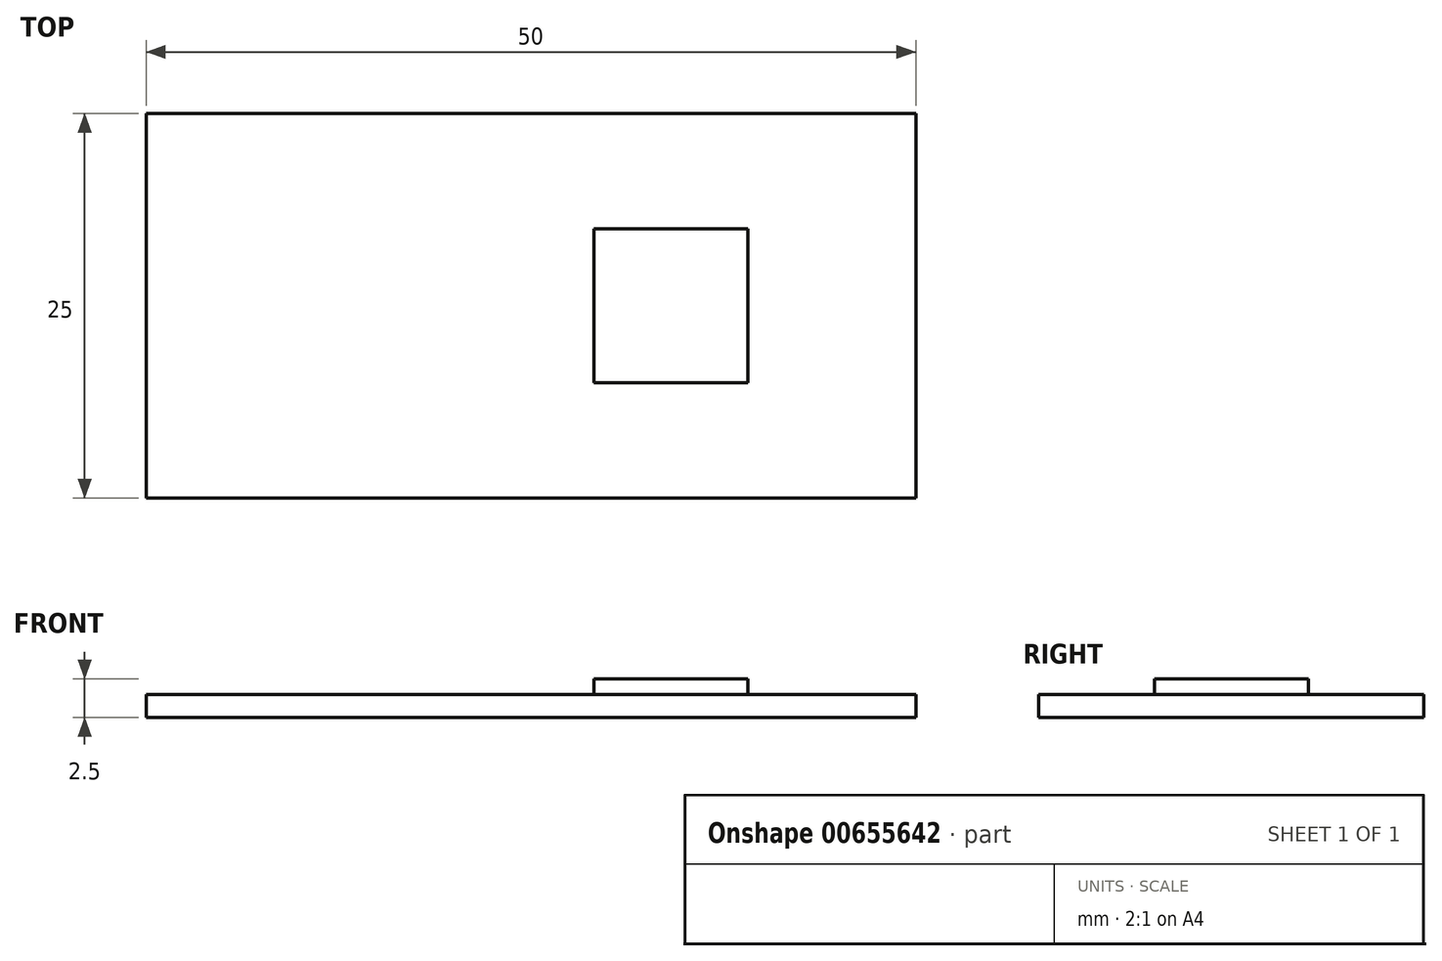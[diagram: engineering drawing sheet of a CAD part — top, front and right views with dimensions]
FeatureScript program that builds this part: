
annotation { "Feature Type Name" : "Feature", "Feature Type Description" : "" }
export const myFeature = defineFeature(function(context is Context, id is Id, definition is map)
    precondition{}
    {
        {
            var Q0;
            Q0=qCreatedBy(makeId("Top.planeOp"),FACE);
            var sketch = newSketch(context, id + "F0", { "sketchPlane" : qUnion([Q0])});
            skLineSegment(sketch, "E0.bottom", {"start": v(25, -12.5) * mm, "end": v(-25, -12.5) * mm});
            skLineSegment(sketch, "E0.top", {"start": v(25, 12.5) * mm, "end": v(-25, 12.5) * mm});
            skLineSegment(sketch, "E0.left", {"start": v(25, -12.5) * mm, "end": v(25, 12.5) * mm});
            skLineSegment(sketch, "E0.right", {"start": v(-25, -12.5) * mm, "end": v(-25, 12.5) * mm});
            skPoint(sketch, "E0.middle", {"position": v(0, 0) * mm});
            skSolve(sketch);
        }
        {
            var Q0;
            Q0=makeQuery(id+"F0.imprint","IMPRINT",FACE,{"disambiguationData":[TD([[makeQuery(id+"F0.imprint","IMPRINT",EDGE,{"derivedFrom":sQuery(id+"F0.wireOp",EDGE,"E0.bottom")}),-1.0]])]});
            extrude(context, id + "F1", {"entities" : qUnion([Q0]), "depth" : 1.5 * mm, "offsetDistance" : 25 * mm});
        }
        {
            var Q0;
            Q0=makeQuery(id+"F1.opExtrude","CAP_FACE",FACE,{"disambiguationData":[OSD([sQuery(id+"F0.wireOp",EDGE,"E0.bottom"),sQuery(id+"F0.wireOp",EDGE,"E0.top"),sQuery(id+"F0.wireOp",EDGE,"E0.left"),sQuery(id+"F0.wireOp",EDGE,"E0.right")])],"isStart":false});
            var sketch = newSketch(context, id + "F2", { "sketchPlane" : qUnion([Q0])});
            skLineSegment(sketch, "E1", {"start": v(-25, 0) * mm, "end": v(25, 0) * mm});
            skLineSegment(sketch, "E2.bottom", {"start": v(14.1, -5) * mm, "end": v(4.1, -5) * mm});
            skLineSegment(sketch, "E2.top", {"start": v(14.1, 5) * mm, "end": v(4.1, 5) * mm});
            skLineSegment(sketch, "E2.left", {"start": v(14.1, -5) * mm, "end": v(14.1, 5) * mm});
            skLineSegment(sketch, "E2.right", {"start": v(4.1, -5) * mm, "end": v(4.1, 5) * mm});
            skPoint(sketch, "E2.middle", {"position": v(9.1, 0) * mm});
            skSolve(sketch);
        }
        {
            var Q0;
            {var subQ5=sQuery(id+"F2.wireOp",EDGE,"E2.top");Q0=makeQuery(id+"F2.imprint","IMPRINT",FACE,{"disambiguationData":[TD([[makeQuery(id+"F2.imprint","IMPRINT",EDGE,{"derivedFrom":subQ5}),1.0]])]});}
            var Q1;
            {var subQ5=sQuery(id+"F2.wireOp",EDGE,"E2.bottom");Q1=makeQuery(id+"F2.imprint","IMPRINT",FACE,{"disambiguationData":[TD([[makeQuery(id+"F2.imprint","IMPRINT",EDGE,{"derivedFrom":subQ5}),-1.0]])]});}
            extrude(context, id + "F3", {"entities" : qUnion([Q0, Q1]), "operationType" : NewBodyOperationType.ADD, "depth" : 1 * mm, "offsetDistance" : 25 * mm});
        }
    });
